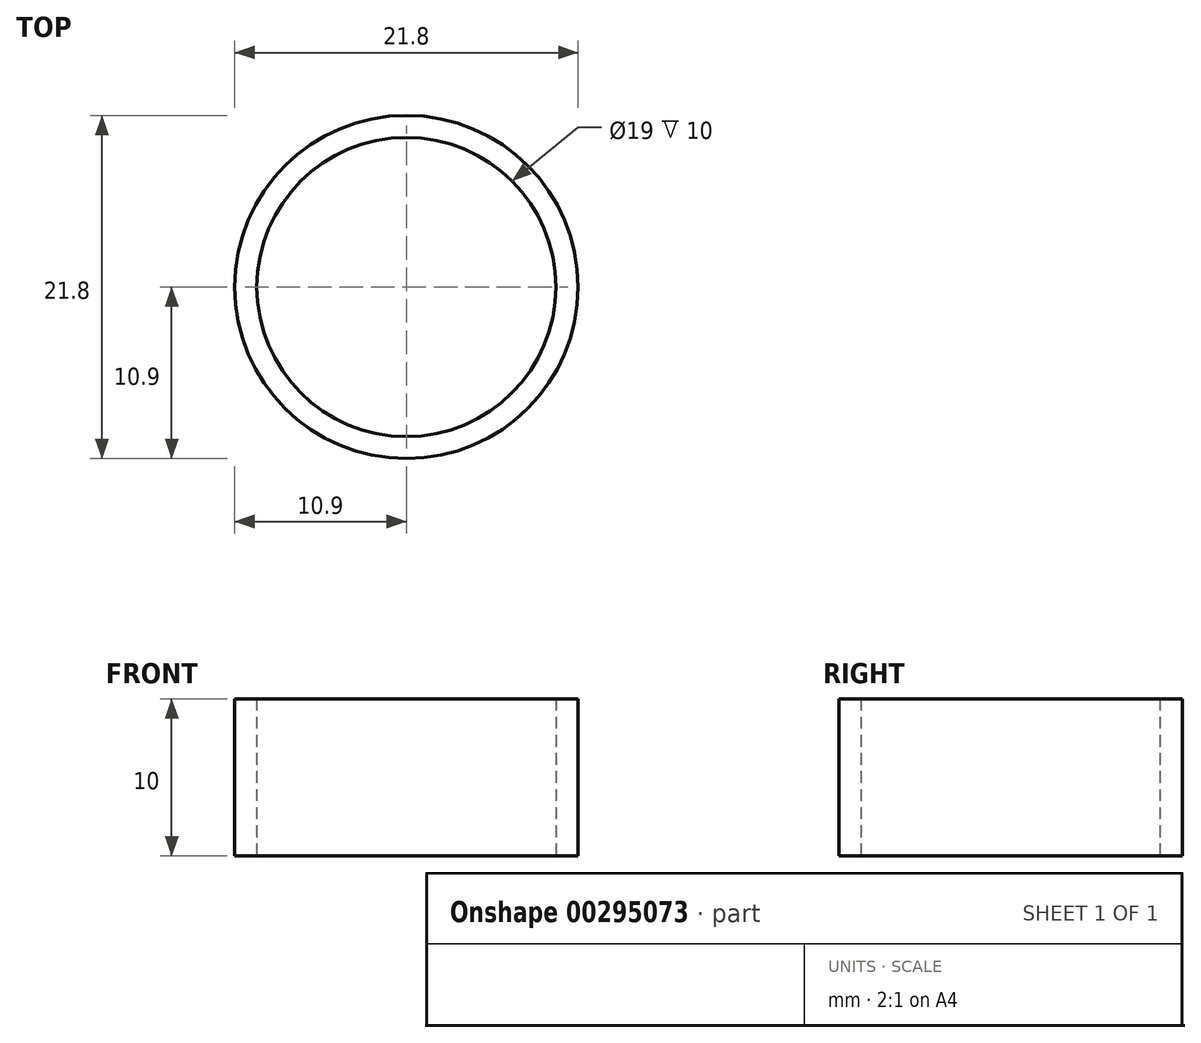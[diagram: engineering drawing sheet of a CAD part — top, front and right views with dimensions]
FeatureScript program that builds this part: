
annotation { "Feature Type Name" : "Feature", "Feature Type Description" : "" }
export const myFeature = defineFeature(function(context is Context, id is Id, definition is map)
    precondition{}
    {
        {
            var Q0;
            Q0=qCreatedBy(makeId("Top.planeOp"),FACE);
            var sketch = newSketch(context, id + "F0", { "sketchPlane" : qUnion([Q0])});
            skCircle(sketch, "E0", {"center": v(0, 0) * mm, "radius": 10.9 * mm});
            skCircle(sketch, "E1", {"center": v(0, 0) * mm, "radius": 9.5 * mm});
            skSolve(sketch);
        }
        {
            var Q0;
            Q0 = qSketchRegion(id + "F0", true);
            extrude(context, id + "F1", {"entities" : qUnion([Q0]), "depth" : 10 * mm});
        }
    });
